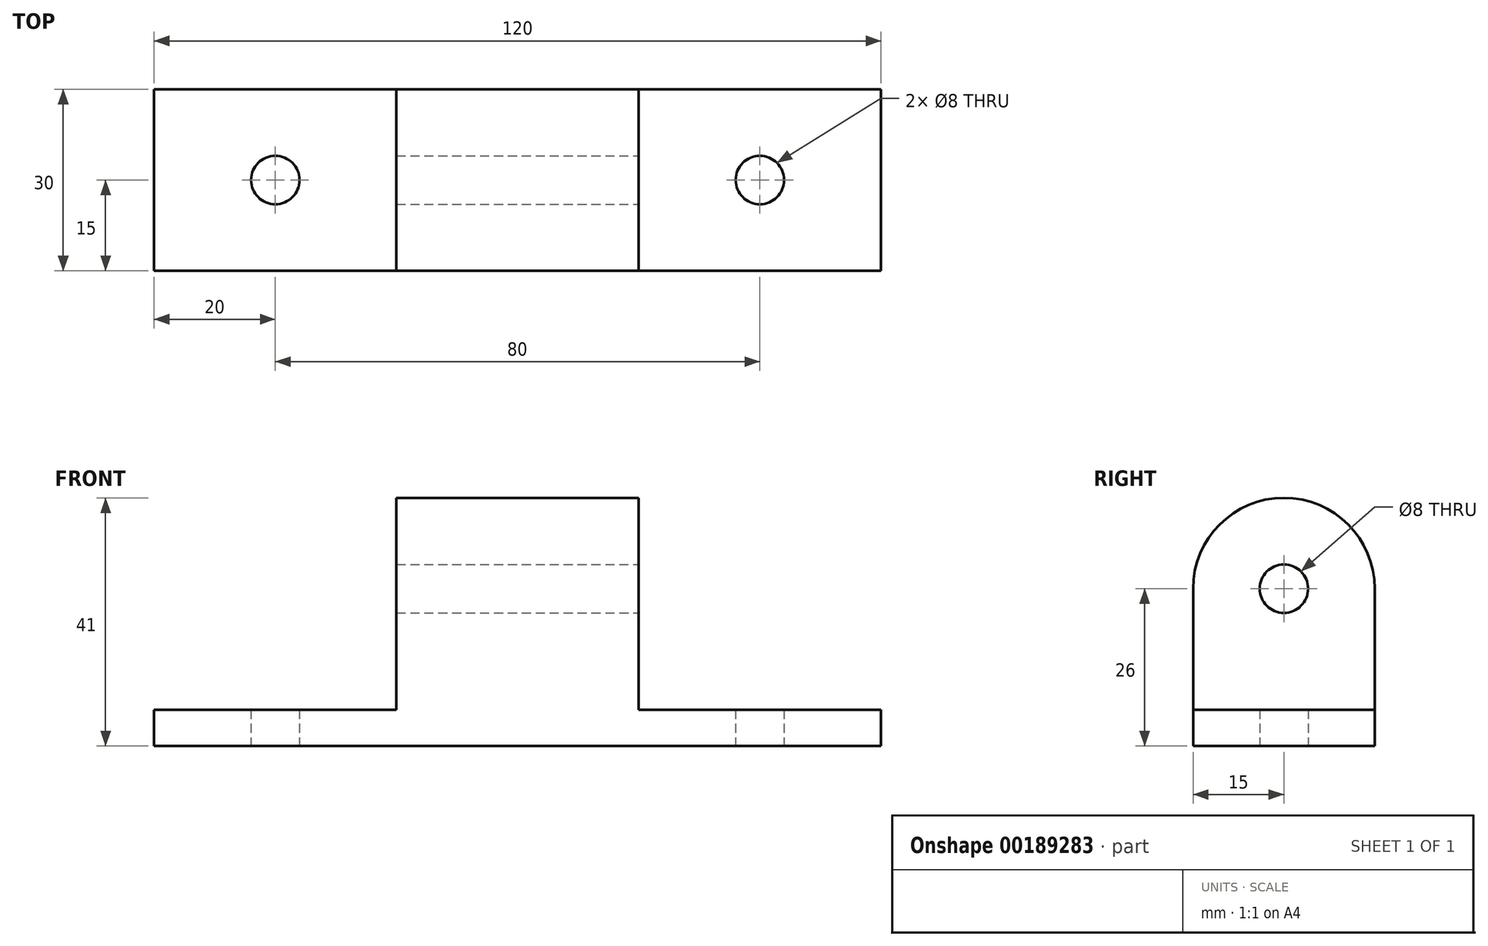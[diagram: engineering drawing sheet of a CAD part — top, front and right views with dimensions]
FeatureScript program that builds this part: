
annotation { "Feature Type Name" : "Feature", "Feature Type Description" : "" }
export const myFeature = defineFeature(function(context is Context, id is Id, definition is map)
    precondition{}
    {
        {
            var Q0;
            Q0=qCreatedBy(makeId("Top.planeOp"),FACE);
            var sketch = newSketch(context, id + "F0", { "sketchPlane" : qUnion([Q0])});
            skLineSegment(sketch, "E0.bottom", {"start": v(60, -15) * mm, "end": v(-60, -15) * mm});
            skLineSegment(sketch, "E0.top", {"start": v(60, 15) * mm, "end": v(-60, 15) * mm});
            skLineSegment(sketch, "E0.left", {"start": v(60, -15) * mm, "end": v(60, 15) * mm});
            skLineSegment(sketch, "E0.right", {"start": v(-60, -15) * mm, "end": v(-60, 15) * mm});
            skPoint(sketch, "E0.middle", {"position": v(0, 0) * mm});
            skLineSegment(sketch, "E1", {"start": v(0, 15) * mm, "end": v(-20, 15) * mm});
            skLineSegment(sketch, "E2", {"start": v(0, -15) * mm, "end": v(20, -15) * mm});
            skCircle(sketch, "E3", {"center": v(-40, 0) * mm, "radius": 4 * mm});
            skCircle(sketch, "E4", {"center": v(40, 0) * mm, "radius": 4 * mm});
            skSolve(sketch);
        }
        {
            var Q0;
            {var subQ3=sQuery(id+"F0.wireOp",EDGE,"E0.left");Q0=makeQuery(id+"F0.imprint","IMPRINT",FACE,{"disambiguationData":[TD([[makeQuery(id+"F0.imprint","IMPRINT",EDGE,{"derivedFrom":subQ3}),1.0]])]});}
            extrude(context, id + "F1", {"entities" : qUnion([Q0]), "depth" : 6 * mm});
        }
        {
            var Q0;
            Q0=makeQuery(id+"F1.opExtrude","CAP_FACE",FACE,{"disambiguationData":[OSD([sQuery(id+"F0.wireOp",EDGE,"E0.bottom"),sQuery(id+"F0.wireOp",EDGE,"E0.top"),sQuery(id+"F0.wireOp",EDGE,"E0.left"),sQuery(id+"F0.wireOp",EDGE,"E0.right"),sQuery(id+"F0.wireOp",EDGE,"E1"),sQuery(id+"F0.wireOp",EDGE,"E2")])],"isStart":false});
            var sketch = newSketch(context, id + "F2", { "sketchPlane" : qUnion([Q0])});
            skLineSegment(sketch, "E5", {"start": v(0, 15) * mm, "end": v(-20, 15) * mm});
            skLineSegment(sketch, "E6", {"start": v(-20, 15) * mm, "end": v(-20, -15) * mm});
            skLineSegment(sketch, "E7", {"start": v(-20, -15) * mm, "end": v(20, -15) * mm});
            skLineSegment(sketch, "E8", {"start": v(20, -15) * mm, "end": v(20, 15) * mm});
            skLineSegment(sketch, "E9", {"start": v(20, 15) * mm, "end": v(0, 15) * mm});
            skSolve(sketch);
        }
        {
            var Q0;
            Q0=makeQuery(id+"F2.imprint","IMPRINT",FACE,{"disambiguationData":[TD([[makeQuery(id+"F2.imprint","IMPRINT",EDGE,{"derivedFrom":sQuery(id+"F2.wireOp",EDGE,"E5")}),1.0]])]});
            extrude(context, id + "F3", {"entities" : qUnion([Q0]), "operationType" : NewBodyOperationType.ADD, "depth" : 35 * mm});
        }
        {
            var Q0;
            Q0=makeQuery(id+"F3.opExtrude","SWEPT_FACE",FACE,{"disambiguationData":[OSD([sQuery(id+"F2.wireOp",EDGE,"E8")])]});
            var sketch = newSketch(context, id + "F4", { "sketchPlane" : qUnion([Q0])});
            skLineSegment(sketch, "E10", {"start": v(0, 41) * mm, "end": v(0, 26) * mm});
            skCircle(sketch, "E11", {"center": v(0, 26) * mm, "radius": 15 * mm});
            skLineSegment(sketch, "E12.0", {"start": v(-15, 41) * mm, "end": v(-15, 6) * mm});
            skLineSegment(sketch, "E12.1", {"start": v(-15, 41) * mm, "end": v(15, 41) * mm});
            skLineSegment(sketch, "E12.2", {"start": v(15, 41) * mm, "end": v(15, 6) * mm});
            skCircle(sketch, "E13", {"center": v(0, 26) * mm, "radius": 4 * mm});
            skSolve(sketch);
        }
        {
            var Q0;
            {var subQ0=sQuery(id+"F4.wireOp",EDGE,"E12.1");var subQ1=sQuery(id+"F4.wireOp",EDGE,"E11");var subQ2=makeQuery(id+"F4.imprint","INTERSECT",VERTEX,{"derivedFrom":[subQ1,subQ0]});Q0=makeQuery(id+"F4.imprint","IMPRINT",FACE,{"disambiguationData":[TD([[makeQuery(id+"F4.imprint","IMPRINT",EDGE,{"disambiguationData":[TD([[subQ2,-1.0]])],"derivedFrom":subQ1}),-1.0]])]});}
            var Q1;
            {var subQ0=sQuery(id+"F4.wireOp",EDGE,"E12.1");var subQ1=sQuery(id+"F4.wireOp",EDGE,"E11");var subQ2=makeQuery(id+"F4.imprint","INTERSECT",VERTEX,{"derivedFrom":[subQ1,subQ0]});Q1=makeQuery(id+"F4.imprint","IMPRINT",FACE,{"disambiguationData":[TD([[makeQuery(id+"F4.imprint","IMPRINT",EDGE,{"disambiguationData":[TD([[subQ2,1.0]])],"derivedFrom":subQ1}),-1.0]])]});}
            var Q2;
            Q2=makeQuery(id+"F4.imprint","IMPRINT",FACE,{"disambiguationData":[TD([[makeQuery(id+"F4.imprint","IMPRINT",EDGE,{"derivedFrom":sQuery(id+"F4.wireOp",EDGE,"E13")}),1.0]])]});
            extrude(context, id + "F5", {"entities" : qUnion([Q0, Q1, Q2]), "operationType" : NewBodyOperationType.REMOVE, "oppositeDirection" : true, "depth" : 45 * mm});
        }
    });
